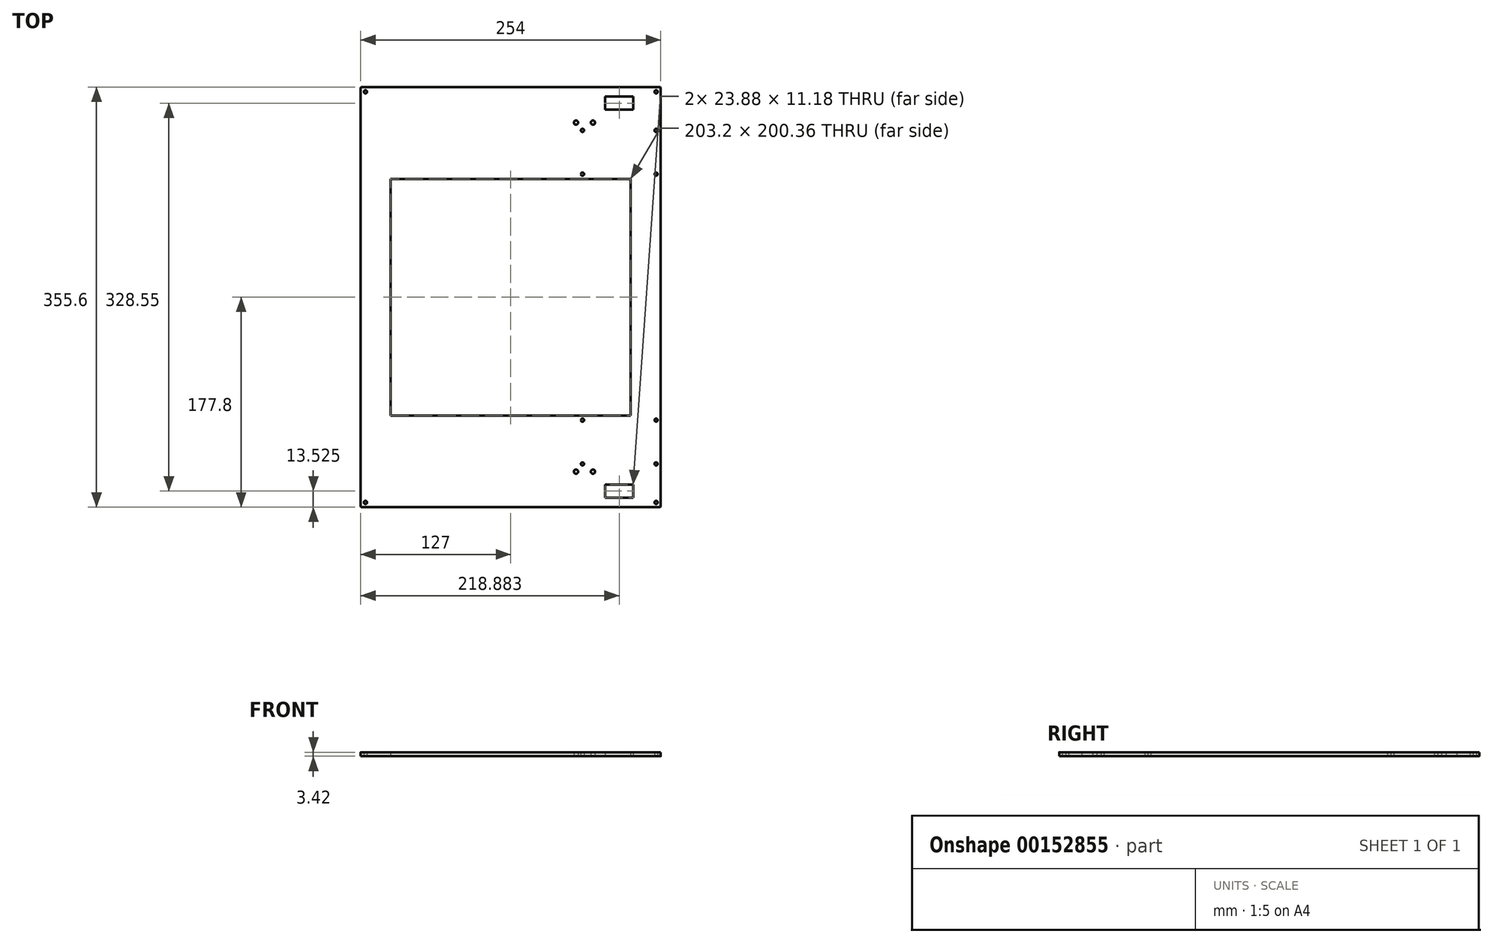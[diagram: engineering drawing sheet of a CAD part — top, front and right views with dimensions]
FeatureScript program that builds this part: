
annotation { "Feature Type Name" : "Feature", "Feature Type Description" : "" }
export const myFeature = defineFeature(function(context is Context, id is Id, definition is map)
    precondition{}
    {
        {
            var Q0;
            Q0=qCreatedBy(makeId("Top.planeOp"),FACE);
            var sketch = newSketch(context, id + "F0", { "sketchPlane" : qUnion([Q0])});
            skLineSegment(sketch, "E0.bottom", {"start": v(127, -177.8) * mm, "end": v(-127, -177.8) * mm});
            skLineSegment(sketch, "E0.top", {"start": v(127, 177.8) * mm, "end": v(-127, 177.8) * mm});
            skLineSegment(sketch, "E0.left", {"start": v(127, -177.8) * mm, "end": v(127, 177.8) * mm});
            skLineSegment(sketch, "E0.right", {"start": v(-127, -177.8) * mm, "end": v(-127, 177.8) * mm});
            skPoint(sketch, "E0.middle", {"position": v(0, 0) * mm});
            skLineSegment(sketch, "E1.bottom", {"start": v(-123.03, 173.83) * mm, "end": v(123.03, 173.83) * mm, "construction": true});
            skLineSegment(sketch, "E1.top", {"start": v(-123.03, -173.83) * mm, "end": v(123.03, -173.83) * mm, "construction": true});
            skLineSegment(sketch, "E1.left", {"start": v(-123.03, 173.83) * mm, "end": v(-123.03, -173.83) * mm, "construction": true});
            skLineSegment(sketch, "E1.right", {"start": v(123.03, 173.83) * mm, "end": v(123.03, -173.83) * mm, "construction": true});
            skLineSegment(sketch, "E2", {"start": v(-123.03, 173.83) * mm, "end": v(-127, 173.83) * mm, "construction": true});
            skLineSegment(sketch, "E3", {"start": v(-123.03, 173.83) * mm, "end": v(-123.03, 177.8) * mm, "construction": true});
            skCircle(sketch, "E4", {"center": v(-123.03, 173.83) * mm, "radius": 1.35 * mm});
            skCircle(sketch, "E5", {"center": v(123.03, 173.83) * mm, "radius": 1.35 * mm});
            skCircle(sketch, "E6", {"center": v(-123.03, -173.83) * mm, "radius": 1.35 * mm});
            skCircle(sketch, "E7", {"center": v(123.03, -173.83) * mm, "radius": 1.35 * mm});
            skLineSegment(sketch, "E8.bottom", {"start": v(-101.6, 100.18) * mm, "end": v(101.6, 100.18) * mm});
            skLineSegment(sketch, "E8.top", {"start": v(-101.6, -100.18) * mm, "end": v(101.6, -100.18) * mm});
            skLineSegment(sketch, "E8.left", {"start": v(-101.6, 100.18) * mm, "end": v(-101.6, -100.18) * mm});
            skLineSegment(sketch, "E8.right", {"start": v(101.6, 100.18) * mm, "end": v(101.6, -100.18) * mm});
            skLineSegment(sketch, "E9", {"start": v(-101.6, 100.18) * mm, "end": v(-123.03, 100.18) * mm, "construction": true});
            skLineSegment(sketch, "E10", {"start": v(-101.6, 100.18) * mm, "end": v(-101.6, 173.83) * mm, "construction": true});
            skLineSegment(sketch, "E11", {"start": v(101.6, 100.18) * mm, "end": v(101.6, 147.74) * mm, "construction": true});
            skLineSegment(sketch, "E12", {"start": v(101.6, 147.74) * mm, "end": v(69.6, 147.74) * mm, "construction": true});
            skLineSegment(sketch, "E13", {"start": v(69.6, 147.74) * mm, "end": v(55.24, 147.74) * mm, "construction": true});
            skLineSegment(sketch, "E14", {"start": v(101.6, -100.18) * mm, "end": v(101.6, -147.74) * mm, "construction": true});
            skLineSegment(sketch, "E15", {"start": v(101.6, -147.74) * mm, "end": v(69.6, -147.74) * mm, "construction": true});
            skLineSegment(sketch, "E16", {"start": v(69.6, -147.74) * mm, "end": v(55.24, -147.74) * mm, "construction": true});
            skCircle(sketch, "E17", {"center": v(55.24, -147.74) * mm, "radius": 1.83 * mm});
            skCircle(sketch, "E18", {"center": v(69.6, -147.74) * mm, "radius": 1.83 * mm});
            skCircle(sketch, "E19", {"center": v(69.6, 147.74) * mm, "radius": 1.83 * mm});
            skCircle(sketch, "E20", {"center": v(55.24, 147.74) * mm, "radius": 1.83 * mm});
            skLineSegment(sketch, "E21.bottom", {"start": v(79.95, 169.86) * mm, "end": v(103.82, 169.86) * mm});
            skLineSegment(sketch, "E21.top", {"start": v(79.95, 158.69) * mm, "end": v(103.82, 158.69) * mm});
            skLineSegment(sketch, "E21.left", {"start": v(79.95, 169.86) * mm, "end": v(79.95, 158.69) * mm});
            skLineSegment(sketch, "E21.right", {"start": v(103.82, 169.86) * mm, "end": v(103.82, 158.69) * mm});
            skLineSegment(sketch, "E22.bottom", {"start": v(79.95, -169.86) * mm, "end": v(103.82, -169.86) * mm});
            skLineSegment(sketch, "E22.top", {"start": v(79.95, -158.69) * mm, "end": v(103.82, -158.69) * mm});
            skLineSegment(sketch, "E22.left", {"start": v(79.95, -169.86) * mm, "end": v(79.95, -158.69) * mm});
            skLineSegment(sketch, "E22.right", {"start": v(103.82, -169.86) * mm, "end": v(103.82, -158.69) * mm});
            skLineSegment(sketch, "E23", {"start": v(91.88, 169.86) * mm, "end": v(91.88, 173.83) * mm, "construction": true});
            skLineSegment(sketch, "E24", {"start": v(91.88, -169.86) * mm, "end": v(91.88, -173.83) * mm, "construction": true});
            skLineSegment(sketch, "E25", {"start": v(91.88, 158.69) * mm, "end": v(91.88, 141.2) * mm, "construction": true});
            skLineSegment(sketch, "E26", {"start": v(91.88, -158.69) * mm, "end": v(91.88, -141.2) * mm, "construction": true});
            skLineSegment(sketch, "E27.bottom", {"start": v(60.73, -141.2) * mm, "end": v(123.03, -141.2) * mm, "construction": true});
            skLineSegment(sketch, "E27.top", {"start": v(60.73, -104.15) * mm, "end": v(123.03, -104.15) * mm, "construction": true});
            skLineSegment(sketch, "E27.left", {"start": v(60.73, -141.2) * mm, "end": v(60.73, -104.15) * mm, "construction": true});
            skLineSegment(sketch, "E27.right", {"start": v(123.03, -141.2) * mm, "end": v(123.03, -104.15) * mm, "construction": true});
            skLineSegment(sketch, "E28.bottom", {"start": v(60.73, 141.2) * mm, "end": v(123.03, 141.2) * mm, "construction": true});
            skLineSegment(sketch, "E28.top", {"start": v(60.73, 104.15) * mm, "end": v(123.03, 104.15) * mm, "construction": true});
            skLineSegment(sketch, "E28.left", {"start": v(60.73, 141.2) * mm, "end": v(60.73, 104.15) * mm, "construction": true});
            skLineSegment(sketch, "E28.right", {"start": v(123.03, 141.2) * mm, "end": v(123.03, 104.15) * mm, "construction": true});
            skCircle(sketch, "E29", {"center": v(60.73, -141.2) * mm, "radius": 1.35 * mm});
            skCircle(sketch, "E30", {"center": v(123.03, -141.2) * mm, "radius": 1.35 * mm});
            skCircle(sketch, "E31", {"center": v(123.03, -104.15) * mm, "radius": 1.35 * mm});
            skCircle(sketch, "E32", {"center": v(60.73, -104.15) * mm, "radius": 1.35 * mm});
            skCircle(sketch, "E33", {"center": v(60.73, 141.2) * mm, "radius": 1.35 * mm});
            skCircle(sketch, "E34", {"center": v(123.03, 141.2) * mm, "radius": 1.35 * mm});
            skCircle(sketch, "E35", {"center": v(123.03, 104.15) * mm, "radius": 1.35 * mm});
            skCircle(sketch, "E36", {"center": v(60.73, 104.15) * mm, "radius": 1.35 * mm});
            skLineSegment(sketch, "E37", {"start": v(91.88, 104.15) * mm, "end": v(91.88, 100.18) * mm, "construction": true});
            skLineSegment(sketch, "E38", {"start": v(91.88, 144.47) * mm, "end": v(91.88, 141.2) * mm, "construction": true});
            skLineSegment(sketch, "E39", {"start": v(62.42, 144.47) * mm, "end": v(91.88, 144.47) * mm, "construction": true});
            skLineSegment(sketch, "E40", {"start": v(62.42, 147.74) * mm, "end": v(62.42, 144.47) * mm, "construction": true});
            skSolve(sketch);
        }
        {
            var Q0;
            Q0=qSketchRegion(id+"F0",true);
            extrude(context, id + "F1", {"entities" : qUnion([Q0]), "depth" : 3.42 * mm});
        }
        {
            var Q0;
            Q0=makeQuery(id+"F1.opExtrude","SWEPT_EDGE",EDGE,{"disambiguationData":[OSD([sQuery(id+"F0.wireOp",EDGE,"E0.bottom"),sQuery(id+"F0.wireOp",EDGE,"E0.right")])]});
            var Q1;
            Q1=makeQuery(id+"F1.opExtrude","SWEPT_EDGE",EDGE,{"disambiguationData":[OSD([sQuery(id+"F0.wireOp",EDGE,"E0.bottom"),sQuery(id+"F0.wireOp",EDGE,"E0.left")])]});
            var Q2;
            Q2=makeQuery(id+"F1.opExtrude","SWEPT_EDGE",EDGE,{"disambiguationData":[OSD([sQuery(id+"F0.wireOp",EDGE,"E0.top"),sQuery(id+"F0.wireOp",EDGE,"E0.left")])]});
            var Q3;
            Q3=makeQuery(id+"F1.opExtrude","SWEPT_EDGE",EDGE,{"disambiguationData":[OSD([sQuery(id+"F0.wireOp",EDGE,"E0.top"),sQuery(id+"F0.wireOp",EDGE,"E0.right")])]});
            fillet(context, id + "F2", {"entities" : qUnion([Q0, Q1, Q2, Q3]), "radius" : 0.76 * mm, "tangentPropagation" : true, "allowEdgeOverflow" : false});
        }
    });
